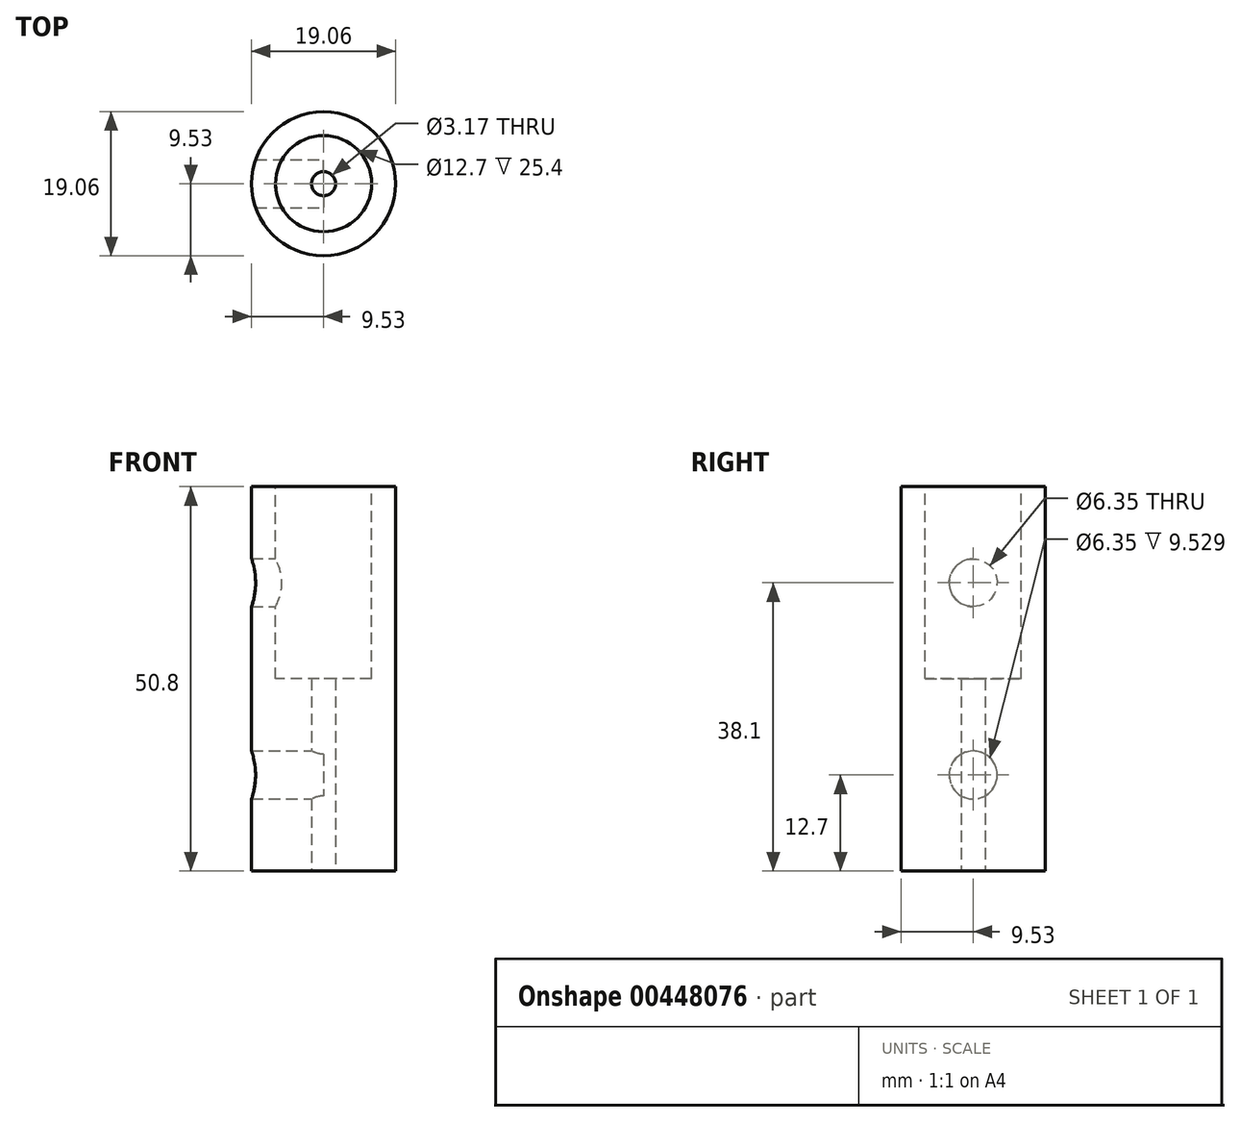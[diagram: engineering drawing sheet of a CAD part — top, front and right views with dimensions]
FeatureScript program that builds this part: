
annotation { "Feature Type Name" : "Feature", "Feature Type Description" : "" }
export const myFeature = defineFeature(function(context is Context, id is Id, definition is map)
    precondition{}
    {
        {
            var Q0;
            Q0=qCreatedBy(makeId("Top.planeOp"),FACE);
            var sketch = newSketch(context, id + "F0", { "sketchPlane" : qUnion([Q0])});
            skCircle(sketch, "E0", {"center": v(0, 0) * mm, "radius": 1.59 * mm});
            skCircle(sketch, "E1", {"center": v(0, 0) * mm, "radius": 9.53 * mm});
            skSolve(sketch);
        }
        {
            var Q0;
            Q0 = qSketchRegion(id + "F0", true);
            extrude(context, id + "F1", {"entities" : qUnion([Q0]), "depth" : 50.8 * mm});
        }
        {
            var Q0;
            Q0=makeQuery(id+"F1.opExtrude","CAP_FACE",FACE,{"disambiguationData":[OSD([sQuery(id+"F0.wireOp",EDGE,"E0"),sQuery(id+"F0.wireOp",EDGE,"E1")])],"isStart":false});
            var sketch = newSketch(context, id + "F2", { "sketchPlane" : qUnion([Q0])});
            skCircle(sketch, "E2", {"center": v(0, 0) * mm, "radius": 6.35 * mm});
            skSolve(sketch);
        }
        {
            var Q0;
            Q0 = qSketchRegion(id + "F2", true);
            extrude(context, id + "F3", {"entities" : qUnion([Q0]), "operationType" : NewBodyOperationType.REMOVE, "oppositeDirection" : true, "depth" : 25.4 * mm});
        }
        {
            var Q0;
            Q0=qCreatedBy(makeId("Right.planeOp"),FACE);
            var sketch = newSketch(context, id + "F4", { "sketchPlane" : qUnion([Q0])});
            skCircle(sketch, "E3", {"center": v(0, 12.7) * mm, "radius": 3.18 * mm});
            skCircle(sketch, "E4", {"center": v(0, 38.1) * mm, "radius": 3.18 * mm});
            skSolve(sketch);
        }
        {
            var Q0;
            Q0 = qSketchRegion(id + "F4", true);
            extrude(context, id + "F5", {"entities" : qUnion([Q0]), "operationType" : NewBodyOperationType.REMOVE, "endBound" : BoundingType.THROUGH_ALL, "oppositeDirection" : true, "depth" : 25.4 * mm});
        }
    });
